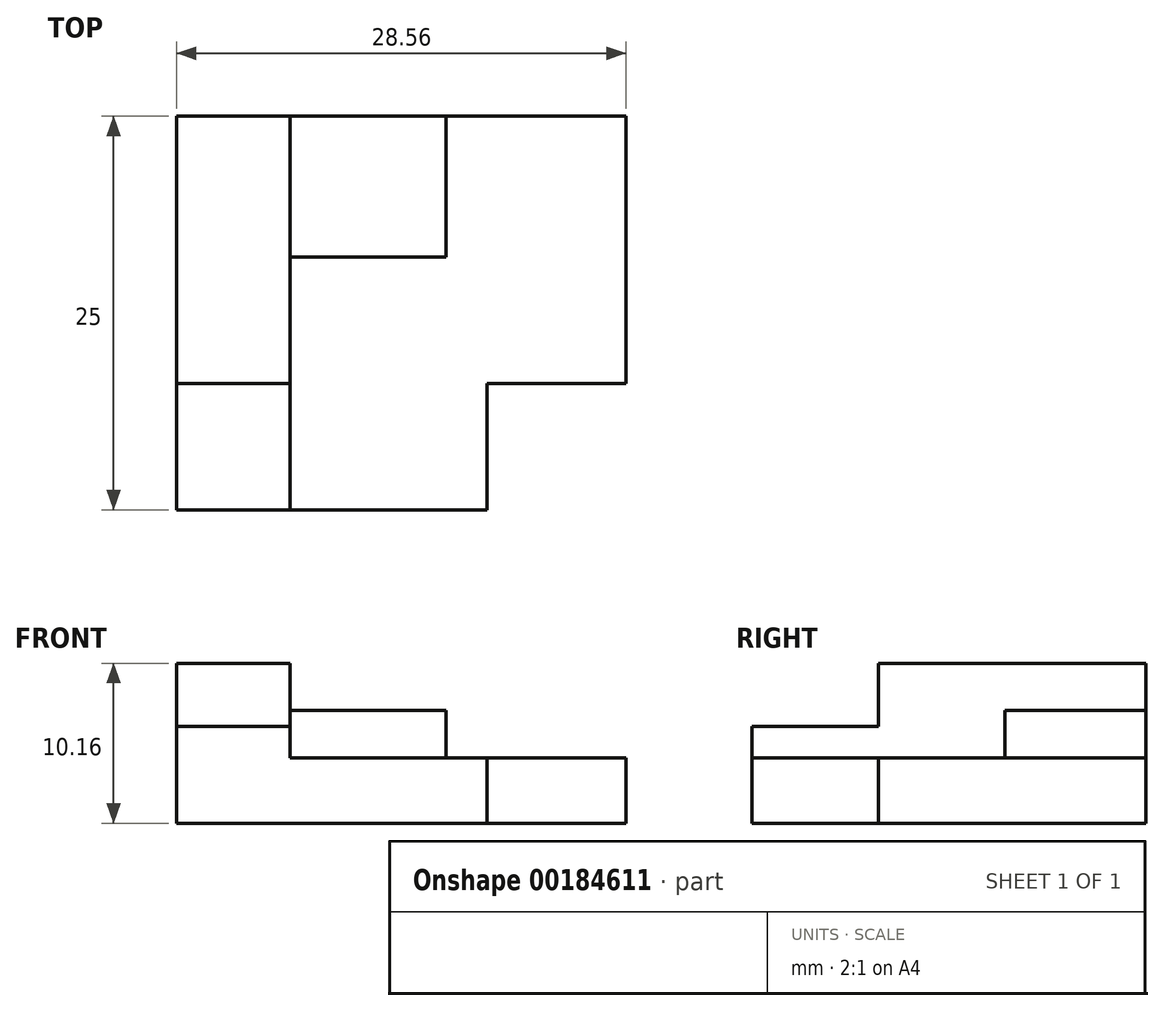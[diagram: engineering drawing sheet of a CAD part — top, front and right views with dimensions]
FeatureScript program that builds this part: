
annotation { "Feature Type Name" : "Feature", "Feature Type Description" : "" }
export const myFeature = defineFeature(function(context is Context, id is Id, definition is map)
    precondition{}
    {
        {
            var Q0;
            Q0=qCreatedBy(makeId("Front.planeOp"),FACE);
            var sketch = newSketch(context, id + "F0", { "sketchPlane" : qUnion([Q0])});
            skLineSegment(sketch, "E0.bottom", {"start": v(-10.77, 10.16) * mm, "end": v(12.09, 10.16) * mm});
            skLineSegment(sketch, "E0.top", {"start": v(-10.77, 0) * mm, "end": v(12.09, 0) * mm});
            skLineSegment(sketch, "E0.left", {"start": v(-10.77, 10.16) * mm, "end": v(-10.77, 0) * mm});
            skLineSegment(sketch, "E0.right", {"start": v(12.09, 10.16) * mm, "end": v(12.09, 0) * mm});
            skSolve(sketch);
        }
        {
            var Q0;
            Q0=makeQuery(id+"F0.imprint","IMPRINT",FACE,{"disambiguationData":[TD([[makeQuery(id+"F0.imprint","IMPRINT",EDGE,{"derivedFrom":sQuery(id+"F0.wireOp",EDGE,"iy2yK9mg-o8sJ-MUA5-Od27-95wDPTka7na5.bottom")}),-1.0]])]});
            var Q1;
            Q1=makeQuery(id+"F0.imprint","IMPRINT",FACE,{"disambiguationData":[TD([[makeQuery(id+"F0.imprint","IMPRINT",EDGE,{"derivedFrom":sQuery(id+"F0.wireOp",EDGE,"E0.top")}),1.0]])]});
            extrude(context, id + "F1", {"entities" : qUnion([Q0, Q1]), "depth" : 25 * mm});
        }
        {
            var Q0;
            Q0=makeQuery(id+"F1.opExtrude","SWEPT_FACE",FACE,{"disambiguationData":[OSD([sQuery(id+"F0.wireOp",EDGE,"E0.bottom"),sQuery(id+"F0.wireOp",EDGE,"iy2yK9mg-o8sJ-MUA5-Od27-95wDPTka7na5.bottom")])]});
            var sketch = newSketch(context, id + "F2", { "sketchPlane" : qUnion([Q0])});
            skLineSegment(sketch, "E1.bottom", {"start": v(-10.77, -19.82) * mm, "end": v(-3.6, -19.82) * mm});
            skLineSegment(sketch, "E1.top", {"start": v(-10.77, -25) * mm, "end": v(-3.6, -25) * mm});
            skLineSegment(sketch, "E1.left", {"start": v(-10.77, -19.82) * mm, "end": v(-10.77, -25) * mm});
            skLineSegment(sketch, "E1.right", {"start": v(-3.6, -19.82) * mm, "end": v(-3.6, -25) * mm});
            skSolve(sketch);
        }
        {
            var Q0;
            Q0=makeQuery(id+"F2.imprint","IMPRINT",FACE,{"disambiguationData":[TD([[makeQuery(id+"F2.imprint","IMPRINT",EDGE,{"derivedFrom":sQuery(id+"F2.wireOp",EDGE,"E1.bottom")}),-1.0]])]});
            extrude(context, id + "F3", {"entities" : qUnion([Q0]), "operationType" : NewBodyOperationType.REMOVE, "oppositeDirection" : true, "depth" : 5 * mm});
        }
        {
            var Q0;
            Q0=makeQuery(id+"F1.opExtrude","SWEPT_FACE",FACE,{"disambiguationData":[OSD([sQuery(id+"F0.wireOp",EDGE,"E0.bottom"),sQuery(id+"F0.wireOp",EDGE,"iy2yK9mg-o8sJ-MUA5-Od27-95wDPTka7na5.bottom")])]});
            var sketch = newSketch(context, id + "F4", { "sketchPlane" : qUnion([Q0])});
            skLineSegment(sketch, "E2.bottom", {"start": v(-3.55, 0) * mm, "end": v(6.36, 0) * mm});
            skLineSegment(sketch, "E2.top", {"start": v(-3.55, -8.93) * mm, "end": v(6.36, -8.93) * mm});
            skLineSegment(sketch, "E2.left", {"start": v(-3.55, 0) * mm, "end": v(-3.55, -8.93) * mm});
            skLineSegment(sketch, "E2.right", {"start": v(6.36, 0) * mm, "end": v(6.36, -8.93) * mm});
            skSolve(sketch);
        }
        {
            var Q0;
            Q0=makeQuery(id+"F4.imprint","IMPRINT",FACE,{"disambiguationData":[TD([[makeQuery(id+"F4.imprint","IMPRINT",EDGE,{"derivedFrom":sQuery(id+"F4.wireOp",EDGE,"E2.bottom")}),-1.0]])]});
            extrude(context, id + "F5", {"entities" : qUnion([Q0]), "operationType" : NewBodyOperationType.REMOVE, "oppositeDirection" : true, "depth" : 3 * mm});
        }
        {
            var Q0;
            Q0=makeQuery(id+"F1.opExtrude","SWEPT_FACE",FACE,{"disambiguationData":[OSD([sQuery(id+"F0.wireOp",EDGE,"E0.bottom"),sQuery(id+"F0.wireOp",EDGE,"iy2yK9mg-o8sJ-MUA5-Od27-95wDPTka7na5.bottom")])]});
            var sketch = newSketch(context, id + "F6", { "sketchPlane" : qUnion([Q0])});
            skLineSegment(sketch, "E3.bottom", {"start": v(-3.55, -8.93) * mm, "end": v(6.7, -8.93) * mm});
            skLineSegment(sketch, "E3.top", {"start": v(-3.55, -25) * mm, "end": v(6.7, -25) * mm});
            skLineSegment(sketch, "E3.left", {"start": v(-3.55, -8.93) * mm, "end": v(-3.55, -25) * mm});
            skLineSegment(sketch, "E3.right", {"start": v(6.7, -8.93) * mm, "end": v(6.7, -25) * mm});
            skSolve(sketch);
        }
        {
            var Q0;
            Q0 = qSketchRegion(id + "F6", true);
            var Q1;
            {var subQ3=sQuery(id+"F6.wireOp",EDGE,"E3.right");Q1=makeQuery(id+"F6.imprint","IMPRINT",FACE,{"disambiguationData":[TD([[makeQuery(id+"F6.imprint","IMPRINT",EDGE,{"derivedFrom":subQ3}),1.0]])]});}
            extrude(context, id + "F7", {"entities" : qUnion([Q0, Q1]), "operationType" : NewBodyOperationType.REMOVE, "oppositeDirection" : true, "depth" : 6 * mm});
        }
        {
            var Q0;
            Q0=makeQuery(id+"F7.boolean.opBoolean","COPY",FACE,{"derivedFrom":makeQuery(id+"F7.opExtrude","CAP_FACE",FACE,{"disambiguationData":[OSD([sQuery(id+"F0.wireOp",EDGE,"E0.bottom"),sQuery(id+"F0.wireOp",EDGE,"E0.right"),sQuery(id+"F0.wireOp",EDGE,"iy2yK9mg-o8sJ-MUA5-Od27-95wDPTka7na5.bottom"),sQuery(id+"F4.wireOp",EDGE,"E2.right"),sQuery(id+"F6.wireOp",EDGE,"E3.bottom"),sQuery(id+"F6.wireOp",EDGE,"E3.top"),sQuery(id+"F6.wireOp",EDGE,"E3.left")])],"isStart":false})});
            var sketch = newSketch(context, id + "F8", { "sketchPlane" : qUnion([Q0])});
            skPoint(sketch, "E4.firstSnap0", {"position": v(-3.55, -16.97) * mm});
            skLineSegment(sketch, "E4.bottom", {"start": v(8.94, -16.97) * mm, "end": v(12.09, -16.97) * mm});
            skLineSegment(sketch, "E4.top", {"start": v(8.94, -25) * mm, "end": v(12.09, -25) * mm});
            skLineSegment(sketch, "E4.left", {"start": v(8.94, -16.97) * mm, "end": v(8.94, -25) * mm});
            skLineSegment(sketch, "E4.right", {"start": v(12.09, -16.97) * mm, "end": v(12.09, -25) * mm});
            skSolve(sketch);
        }
        {
            var Q0;
            Q0=makeQuery(id+"F8.imprint","IMPRINT",FACE,{"disambiguationData":[TD([[makeQuery(id+"F8.imprint","IMPRINT",EDGE,{"derivedFrom":sQuery(id+"F8.wireOp",EDGE,"E4.bottom")}),-1.0]])]});
            extrude(context, id + "F9", {"entities" : qUnion([Q0]), "operationType" : NewBodyOperationType.REMOVE, "oppositeDirection" : true, "depth" : 25 * mm});
        }
        {
            var Q0;
            Q0=makeQuery(id+"F7.boolean.opBoolean","MERGE",FACE,{"derivedFrom":[makeQuery(id+"F5.boolean.opBoolean","COPY",FACE,{"derivedFrom":makeQuery(id+"F5.opExtrude","SWEPT_FACE",FACE,{"disambiguationData":[OSD([sQuery(id+"F4.wireOp",EDGE,"E2.left")])]})}),makeQuery(id+"F7.opExtrude","SWEPT_FACE",FACE,{"disambiguationData":[OSD([sQuery(id+"F6.wireOp",EDGE,"E3.left")])]})]});
            var sketch = newSketch(context, id + "F10", { "sketchPlane" : qUnion([Q0])});
            skPoint(sketch, "E5.firstSnap0", {"position": v(-16.97, 4.16) * mm});
            skLineSegment(sketch, "E5.bottom", {"start": v(-16.97, 10.16) * mm, "end": v(-25, 10.16) * mm});
            skLineSegment(sketch, "E5.top", {"start": v(-16.97, 4.16) * mm, "end": v(-25, 4.16) * mm});
            skLineSegment(sketch, "E5.left", {"start": v(-16.97, 10.16) * mm, "end": v(-16.97, 4.16) * mm});
            skLineSegment(sketch, "E5.right", {"start": v(-25, 10.16) * mm, "end": v(-25, 4.16) * mm});
            skSolve(sketch);
        }
        {
            var Q0;
            Q0=makeQuery(id+"F10.imprint","IMPRINT",FACE,{"disambiguationData":[TD([[makeQuery(id+"F10.imprint","IMPRINT",EDGE,{"derivedFrom":sQuery(id+"F10.wireOp",EDGE,"E5.bottom")}),1.0]])]});
            extrude(context, id + "F11", {"entities" : qUnion([Q0]), "operationType" : NewBodyOperationType.REMOVE, "endBound" : BoundingType.THROUGH_ALL, "oppositeDirection" : true, "depth" : 25 * mm});
        }
        {
            var Q0;
            Q0=makeQuery(id+"F11.boolean.opBoolean","MERGE",FACE,{"derivedFrom":[makeQuery(id+"F7.boolean.opBoolean","COPY",FACE,{"derivedFrom":makeQuery(id+"F7.opExtrude","CAP_FACE",FACE,{"disambiguationData":[OSD([sQuery(id+"F0.wireOp",EDGE,"E0.bottom"),sQuery(id+"F0.wireOp",EDGE,"E0.right"),sQuery(id+"F0.wireOp",EDGE,"iy2yK9mg-o8sJ-MUA5-Od27-95wDPTka7na5.bottom"),sQuery(id+"F4.wireOp",EDGE,"E2.right"),sQuery(id+"F6.wireOp",EDGE,"E3.bottom"),sQuery(id+"F6.wireOp",EDGE,"E3.top"),sQuery(id+"F6.wireOp",EDGE,"E3.left")])],"isStart":false})}),makeQuery(id+"F11.opExtrude","SWEPT_FACE",FACE,{"disambiguationData":[OSD([sQuery(id+"F10.wireOp",EDGE,"E5.top")])]})]});
            var sketch = newSketch(context, id + "F12", { "sketchPlane" : qUnion([Q0])});
            skLineSegment(sketch, "E6", {"start": v(-3.55, -16.97) * mm, "end": v(-3.55, -25) * mm});
            skSolve(sketch);
        }
        {
            var Q0;
            {var subQ0=sQuery(id+"F12.wireOp",EDGE,"E6");Q0=makeQuery(id+"F12.imprint","IMPRINT",FACE,{"disambiguationData":[TD([[makeQuery(id+"F12.imprint","IMPRINT",EDGE,{"derivedFrom":subQ0}),-1.0]])]});}
            extrude(context, id + "F13", {"entities" : qUnion([Q0]), "operationType" : NewBodyOperationType.ADD, "depth" : 2 * mm});
        }
        {
            var Q0;
            Q0=makeQuery(id+"F1.opExtrude","SWEPT_FACE",FACE,{"disambiguationData":[OSD([sQuery(id+"F0.wireOp",EDGE,"E0.right")])]});
            extrude(context, id + "F14", {"entities" : qUnion([Q0]), "operationType" : NewBodyOperationType.ADD, "depth" : 5.7 * mm});
        }
    });
